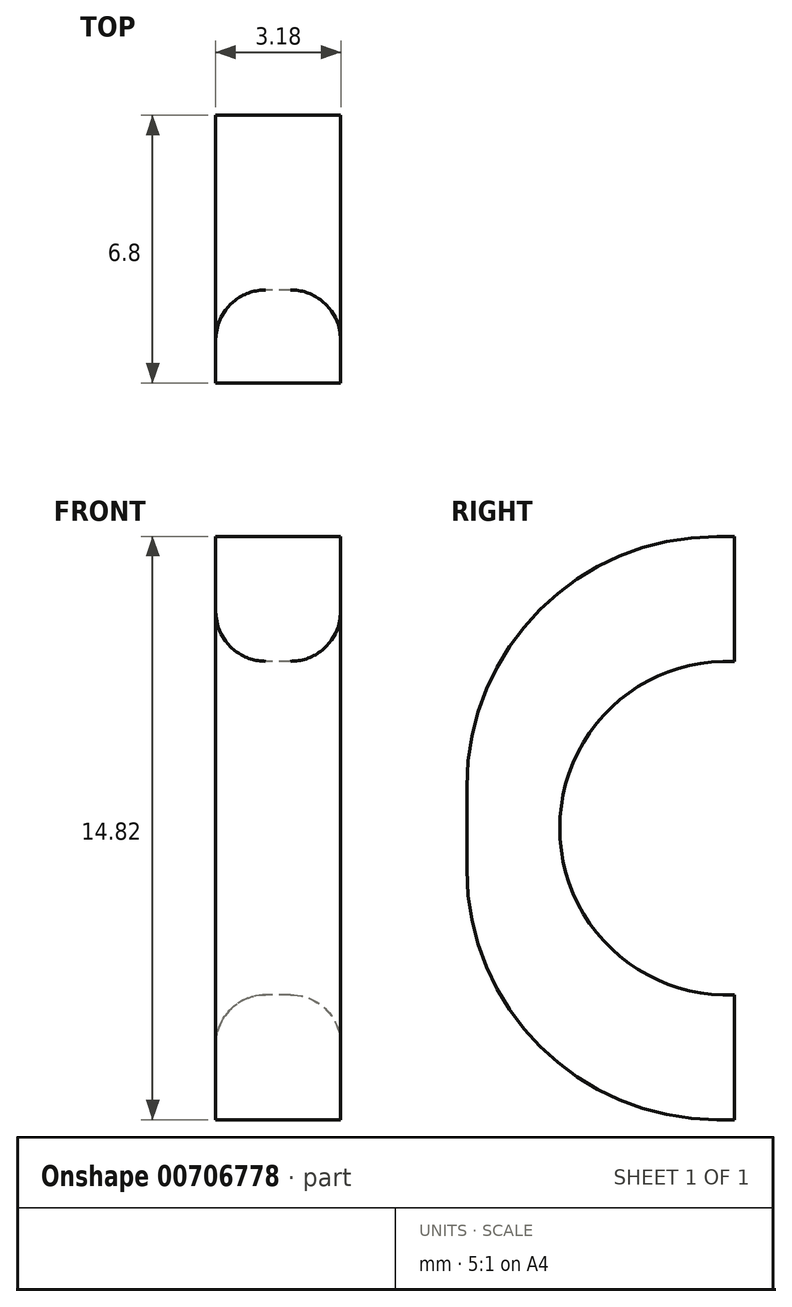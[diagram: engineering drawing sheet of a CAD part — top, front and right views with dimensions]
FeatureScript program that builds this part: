
annotation { "Feature Type Name" : "Feature", "Feature Type Description" : "" }
export const myFeature = defineFeature(function(context is Context, id is Id, definition is map)
    precondition{}
    {
        {
            var Q0;
            Q0=qCreatedBy(makeId("Right.planeOp"),FACE);
            var sketch = newSketch(context, id + "F0", { "sketchPlane" : qUnion([Q0])});
            skLineSegment(sketch, "E0", {"start": v(0, 0) * mm, "end": v(0, 3.18) * mm});
            skLineSegment(sketch, "E1", {"start": v(0, 0) * mm, "end": v(-0.45, 0) * mm});
            skLineSegment(sketch, "E2", {"start": v(-6.8, 6.35) * mm, "end": v(-6.8, 8.47) * mm});
            skLineSegment(sketch, "E3", {"start": v(-0.45, 14.82) * mm, "end": v(0, 14.82) * mm});
            skArc(sketch, "E4", {"start": v(0, 11.64) * mm, "mid": v(-4.44, 7.4) * mm, "end": v(0, 3.18) * mm});
            skPoint(sketch, "E5", {"position": v(0, 7.4) * mm});
            skLineSegment(sketch, "E6.trimOffspring", {"start": v(0, 11.64) * mm, "end": v(0, 14.82) * mm});
            skPoint(sketch, "E7.visualSharp", {"position": v(-6.8, 14.82) * mm});
            skArc(sketch, "E7.filletArc", {"start": v(-0.45, 14.82) * mm, "mid": v(-4.94, 12.96) * mm, "end": v(-6.8, 8.47) * mm});
            skPoint(sketch, "E8.visualSharp", {"position": v(-6.8, 0) * mm});
            skArc(sketch, "E8.filletArc", {"start": v(-6.8, 6.35) * mm, "mid": v(-4.94, 1.86) * mm, "end": v(-0.45, 0) * mm});
            skSolve(sketch);
        }
        {
            var Q0;
            Q0 = qSketchRegion(id + "F0", true);
            extrude(context, id + "F1", {"entities" : qUnion([Q0]), "depth" : 3.17 * mm, "offsetDistance" : 25.4 * mm});
        }
        {
            var Q0;
            Q0=makeQuery(id+"F1.opExtrude","CAP_EDGE",EDGE,{"disambiguationData":[OSD([sQuery(id+"F0.wireOp",EDGE,"E4")])],"isStart":false});
            var Q1;
            Q1=makeQuery(id+"F1.opExtrude","CAP_EDGE",EDGE,{"disambiguationData":[OSD([sQuery(id+"F0.wireOp",EDGE,"E4")])],"isStart":true});
            fillet(context, id + "F2", {"entities" : qUnion([Q0, Q1]), "radius" : 1.27 * mm, "tangentPropagation" : true, "allowEdgeOverflow" : false});
        }
    });
